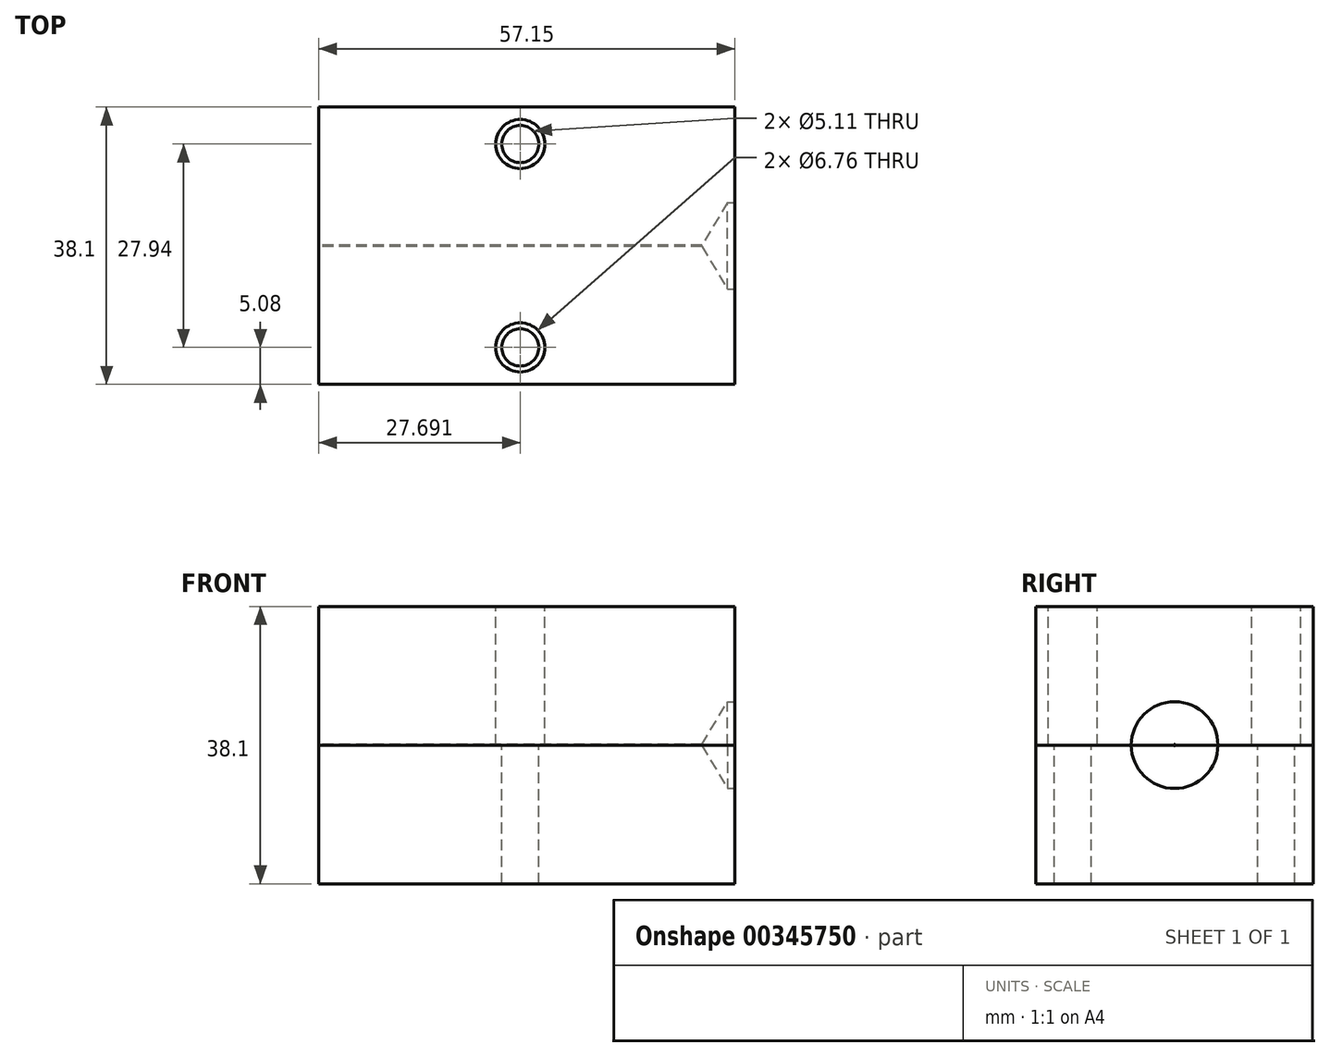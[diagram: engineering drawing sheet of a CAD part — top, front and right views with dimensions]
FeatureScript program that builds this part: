
annotation { "Feature Type Name" : "Feature", "Feature Type Description" : "" }
export const myFeature = defineFeature(function(context is Context, id is Id, definition is map)
    precondition{}
    {
        {
            assignVariable(context, id + "F0", {"name" : "Height", "anyValue" : 38.1 * mm});
        }
        {
            assignVariable(context, id + "F1", {"name" : "TubeDiameter", "anyValue" : 0.18});
        }
        {
            assignVariable(context, id + "F2", {"name" : "ScrewDepth", "anyValue" : 1});
        }
        {
            var Q0;
            Q0=qCreatedBy(makeId("Top.planeOp"),FACE);
            var sketch = newSketch(context, id + "F3", { "sketchPlane" : qUnion([Q0])});
            skLineSegment(sketch, "E0.bottom", {"start": v(28.57, 19.05) * mm, "end": v(-28.58, 19.05) * mm});
            skLineSegment(sketch, "E0.top", {"start": v(28.58, -19.05) * mm, "end": v(-28.57, -19.05) * mm});
            skLineSegment(sketch, "E0.left", {"start": v(28.57, 19.05) * mm, "end": v(28.57, -19.05) * mm});
            skLineSegment(sketch, "E0.right", {"start": v(-28.58, 19.05) * mm, "end": v(-28.57, -19.05) * mm});
            skPoint(sketch, "E0.middle", {"position": v(0, 0) * mm});
            skSolve(sketch);
        }
        {
            var Q0;
            Q0=makeQuery(id+"F3.imprint","IMPRINT",FACE,{"disambiguationData":[TD([[makeQuery(id+"F3.imprint","IMPRINT",EDGE,{"derivedFrom":sQuery(id+"F3.wireOp",EDGE,"E0.bottom")}),1.0]])]});
            extrude(context, id + "F4", {"entities" : qUnion([Q0]), "depth" : getVariable(context, 'Height') / 2});
        }
        {
            var Q0;
            Q0=makeQuery(id+"F3.imprint","IMPRINT",FACE,{"disambiguationData":[TD([[makeQuery(id+"F3.imprint","IMPRINT",EDGE,{"derivedFrom":sQuery(id+"F3.wireOp",EDGE,"E0.bottom")}),1.0]])]});
            extrude(context, id + "F5", {"entities" : qUnion([Q0]), "oppositeDirection" : true, "depth" : getVariable(context, 'Height') / 2});
        }
        {
            var Q0;
            Q0=makeQuery(id+"F4.opExtrude","SWEPT_FACE",FACE,{"disambiguationData":[OSD([sQuery(id+"F3.wireOp",EDGE,"E0.left")])]});
            var sketch = newSketch(context, id + "F6", { "sketchPlane" : qUnion([Q0])});
            skPoint(sketch, "E1", {"position": v(0, 0) * mm});
            skSolve(sketch);
        }
        {
            var Q0;
            Q0=sQuery(id+"F6.wireOp",VERTEX,"E1");
            var Q1;
            Q1=makeQuery(id+"F4.opExtrude","SWEPT_BODY",BODY,{"disambiguationData":[OSD([sQuery(id+"F3.wireOp",EDGE,"E0.bottom"),sQuery(id+"F3.wireOp",EDGE,"E0.top"),sQuery(id+"F3.wireOp",EDGE,"E0.left"),sQuery(id+"F3.wireOp",EDGE,"E0.right")])]});
            var Q2;
            Q2=makeQuery(id+"F5.opExtrude","SWEPT_BODY",BODY,{"disambiguationData":[OSD([sQuery(id+"F3.wireOp",EDGE,"E0.bottom"),sQuery(id+"F3.wireOp",EDGE,"E0.top"),sQuery(id+"F3.wireOp",EDGE,"E0.left"),sQuery(id+"F3.wireOp",EDGE,"E0.right")])]});
            hole(context, id + "F7", {"style" : HoleStyle.SIMPLE, "endStyle" : HoleEndStyle.BLIND, "standardTappedOrClearance" : lookupTablePath({ "standard" : "ANSI", "engagement" : "75%", "pitch" : "28 tpi", "size" : "1/2", "type" : "Tapped" }), "standardBlindInLast" : lookupTablePath({ "standard" : "ANSI", "engagement" : "75%", "pitch" : "28 tpi", "size" : "1/2", "type" : "Tapped" }), "holeDiameter" : 11.9 * mm, "showTappedDepth" : true, "holeDepth" : (getVariable(context, 'ScrewDepth')) * mm, "isTappedThrough" : true, "tappedDepth" : 24.5 * mm, "tapClearance" : 1, "locations" : qUnion([Q0]), "scope" : qUnion([Q1, Q2]), "majorDiameter" : 12.7 * mm});
        }
        {
            var Q0;
            Q0=makeQuery(id+"F4.opExtrude","SWEPT_FACE",FACE,{"disambiguationData":[OSD([sQuery(id+"F3.wireOp",EDGE,"E0.right")])]});
            var sketch = newSketch(context, id + "F8", { "sketchPlane" : qUnion([Q0])});
            skPoint(sketch, "E2", {"position": v(0, 0) * mm});
            skSolve(sketch);
        }
        {
            var Q0;
            Q0=sQuery(id+"F8.wireOp",VERTEX,"E2");
            var Q1;
            Q1=makeQuery(id+"F4.opExtrude","SWEPT_BODY",BODY,{"disambiguationData":[OSD([sQuery(id+"F3.wireOp",EDGE,"E0.bottom"),sQuery(id+"F3.wireOp",EDGE,"E0.top"),sQuery(id+"F3.wireOp",EDGE,"E0.left"),sQuery(id+"F3.wireOp",EDGE,"E0.right")])]});
            var Q2;
            Q2=makeQuery(id+"F5.opExtrude","SWEPT_BODY",BODY,{"disambiguationData":[OSD([sQuery(id+"F3.wireOp",EDGE,"E0.bottom"),sQuery(id+"F3.wireOp",EDGE,"E0.top"),sQuery(id+"F3.wireOp",EDGE,"E0.left"),sQuery(id+"F3.wireOp",EDGE,"E0.right")])]});
            hole(context, id + "F9", {"style" : HoleStyle.SIMPLE, "endStyle" : HoleEndStyle.THROUGH, "holeDiameter" : (getVariable(context, 'TubeDiameter')) * mm, "isTappedThrough" : true, "tappedDepth" : 12 * mm, "tapClearance" : 3, "locations" : qUnion([Q0]), "scope" : qUnion([Q1, Q2])});
        }
        {
            var Q0;
            Q0=makeQuery(id+"F4.opExtrude","CAP_FACE",FACE,{"disambiguationData":[OSD([sQuery(id+"F3.wireOp",EDGE,"E0.bottom"),sQuery(id+"F3.wireOp",EDGE,"E0.top"),sQuery(id+"F3.wireOp",EDGE,"E0.left"),sQuery(id+"F3.wireOp",EDGE,"E0.right")])],"isStart":false});
            var sketch = newSketch(context, id + "F10", { "sketchPlane" : qUnion([Q0])});
            skLineSegment(sketch, "E3", {"start": v(28.57, -13.97) * mm, "end": v(-28.57, -13.97) * mm, "construction": true});
            skLineSegment(sketch, "E4", {"start": v(28.57, 13.97) * mm, "end": v(-28.58, 13.97) * mm, "construction": true});
            skLineSegment(sketch, "E5", {"start": v(-0.89, -19.05) * mm, "end": v(-0.89, 19.05) * mm, "construction": true});
            skPoint(sketch, "E6", {"position": v(-0.89, -13.97) * mm});
            skPoint(sketch, "E7", {"position": v(-0.89, 13.97) * mm});
            skSolve(sketch);
        }
        {
            var Q0;
            Q0=sQuery(id+"F10.wireOp",VERTEX,"E6");
            var Q1;
            Q1=sQuery(id+"F10.wireOp",VERTEX,"E7");
            var Q2;
            Q2=makeQuery(id+"F4.opExtrude","SWEPT_BODY",BODY,{"disambiguationData":[OSD([sQuery(id+"F3.wireOp",EDGE,"E0.bottom"),sQuery(id+"F3.wireOp",EDGE,"E0.top"),sQuery(id+"F3.wireOp",EDGE,"E0.left"),sQuery(id+"F3.wireOp",EDGE,"E0.right")])]});
            hole(context, id + "F11", {"style" : HoleStyle.SIMPLE, "endStyle" : HoleEndStyle.THROUGH, "standardTappedOrClearance" : lookupTablePath({ "standard" : "ANSI", "fit" : "Normal (ASME)", "size" : "1/4", "type" : "Clearance" }), "standardBlindInLast" : lookupTablePath({ "fit" : "Free", "standard" : "ANSI", "size" : "1/4", "type" : "Clearance" }), "holeDiameter" : 6.76 * mm, "tappedDepth" : 12 * mm, "tapClearance" : 3, "locations" : qUnion([Q0, Q1]), "scope" : qUnion([Q2])});
        }
        {
            var Q0;
            {var subQ0=sQuery(id+"F3.wireOp",EDGE,"E0.right");var subQ1=sQuery(id+"F3.wireOp",EDGE,"E0.left");var subQ2=sQuery(id+"F3.wireOp",EDGE,"E0.top");var subQ3=makeQuery(id+"F5.opExtrude","CAP_FACE",FACE,{"disambiguationData":[OSD([sQuery(id+"F3.wireOp",EDGE,"E0.bottom"),subQ2,subQ1,subQ0])],"isStart":true});Q0=makeQuery(id+"F9.hole-0.boolean.opBoolean","SPLIT",FACE,{"disambiguationData":[TD([makeQuery(id+"F5.opExtrude","SWEPT_FACE",FACE,{"disambiguationData":[OSD([subQ2])]})])],"derivedFrom":subQ3});}
            var sketch = newSketch(context, id + "F12", { "sketchPlane" : qUnion([Q0])});
            skLineSegment(sketch, "E8", {"start": v(28.57, -13.97) * mm, "end": v(-28.57, -13.97) * mm, "construction": true});
            skLineSegment(sketch, "E9", {"start": v(28.57, 13.97) * mm, "end": v(-28.58, 13.97) * mm, "construction": true});
            skLineSegment(sketch, "E10", {"start": v(-0.89, -19.05) * mm, "end": v(-0.89, 19.05) * mm, "construction": true});
            skPoint(sketch, "E11", {"position": v(-0.89, -13.97) * mm});
            skPoint(sketch, "E12", {"position": v(-0.89, 13.97) * mm});
            skSolve(sketch);
        }
        {
            var Q0;
            Q0=sQuery(id+"F12.wireOp",VERTEX,"E12");
            var Q1;
            Q1=sQuery(id+"F12.wireOp",VERTEX,"E11");
            var Q2;
            Q2=makeQuery(id+"F5.opExtrude","SWEPT_BODY",BODY,{"disambiguationData":[OSD([sQuery(id+"F3.wireOp",EDGE,"E0.bottom"),sQuery(id+"F3.wireOp",EDGE,"E0.top"),sQuery(id+"F3.wireOp",EDGE,"E0.left"),sQuery(id+"F3.wireOp",EDGE,"E0.right")])]});
            hole(context, id + "F13", {"style" : HoleStyle.SIMPLE, "endStyle" : HoleEndStyle.THROUGH, "standardTappedOrClearance" : lookupTablePath({ "standard" : "ANSI", "engagement" : "75%", "pitch" : "20 tpi", "size" : "1/4", "type" : "Tapped" }), "standardBlindInLast" : lookupTablePath({ "standard" : "ANSI", "engagement" : "75%", "pitch" : "20 tpi", "size" : "1/4", "type" : "Tapped" }), "holeDiameter" : 5.1 * mm, "showTappedDepth" : true, "isTappedThrough" : true, "tappedDepth" : 12 * mm, "tapClearance" : 3, "locations" : qUnion([Q0, Q1]), "scope" : qUnion([Q2]), "majorDiameter" : 6.35 * mm});
        }
    });
